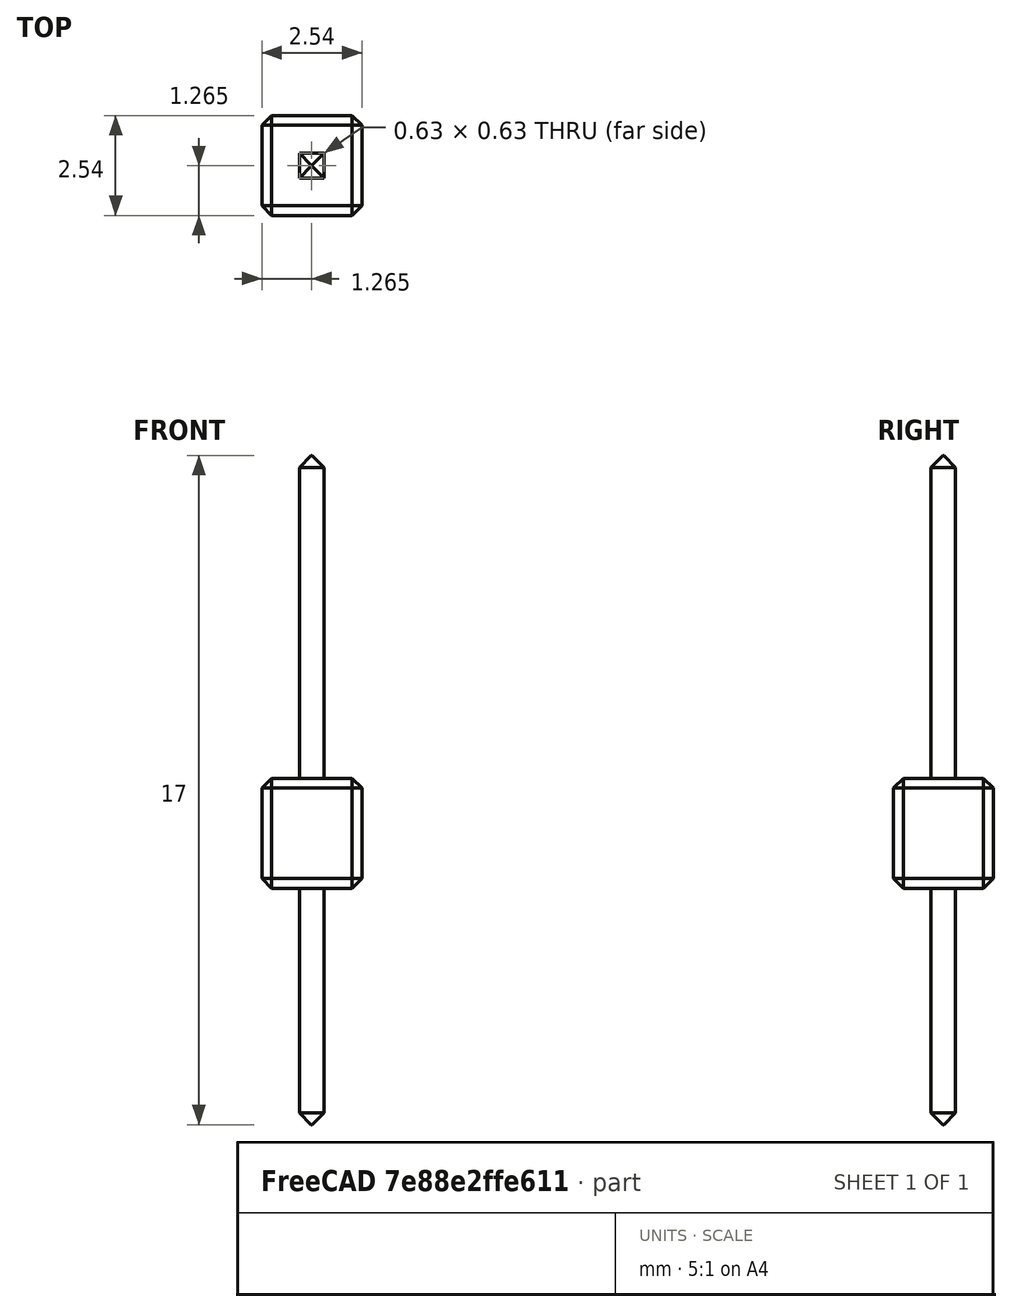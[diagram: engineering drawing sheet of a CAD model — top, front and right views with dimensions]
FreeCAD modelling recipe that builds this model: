
FCSTD DOCUMENT  (FreeCAD 0.18R4 (GitTag))
Label: Single Pin Header
License: All rights reserved
LicenseURL: http://en.wikipedia.org/wiki/All_rights_reserved
objects: Part::Box×2, Part::Chamfer×2, Part::MultiFuse×1
note: 5 computed .brp shape members not serialized (recipe doc carries the construction recipe); baked Part::Feature solids carry a one-line shape summary decoded from their .brp

FEATURE [Part::Box] Box  label="Cube"
  AttacherType = Attacher::AttachEngine3D
  Height = 2.8
  Length = 2.54
  Width = 2.54
FEATURE [Part::Chamfer] Chamfer  label="Body"
  Base = -> Box
  Edges = 12 edges r=0.25: [Edge1,Edge2,Edge3,Edge4,Edge5,Edge6,Edge7,Edge8,Edge9,Edge10,Edge11,Edge12]
FEATURE [Part::Box] Box001  label="Cube001"
  AttacherType = Attacher::AttachEngine3D
  Height = 17
  Length = 0.63
  Placement = pos=(-3,0,0) rot=(0,0,1;0rad)
  Width = 0.63
FEATURE [Part::Chamfer] Chamfer001  label="Pin"
  Base = -> Box001
  Edges = 8 edges r=0.3: [Edge2,Edge4,Edge6,Edge8,Edge9,Edge10,Edge11,Edge12]
  Placement = pos=(3.95,0.95,-6) rot=(0,0,1;0rad)
FEATURE [Part::MultiFuse] Fusion  label="Single Pin"
  Shapes = -> [Chamfer,Chamfer001]
